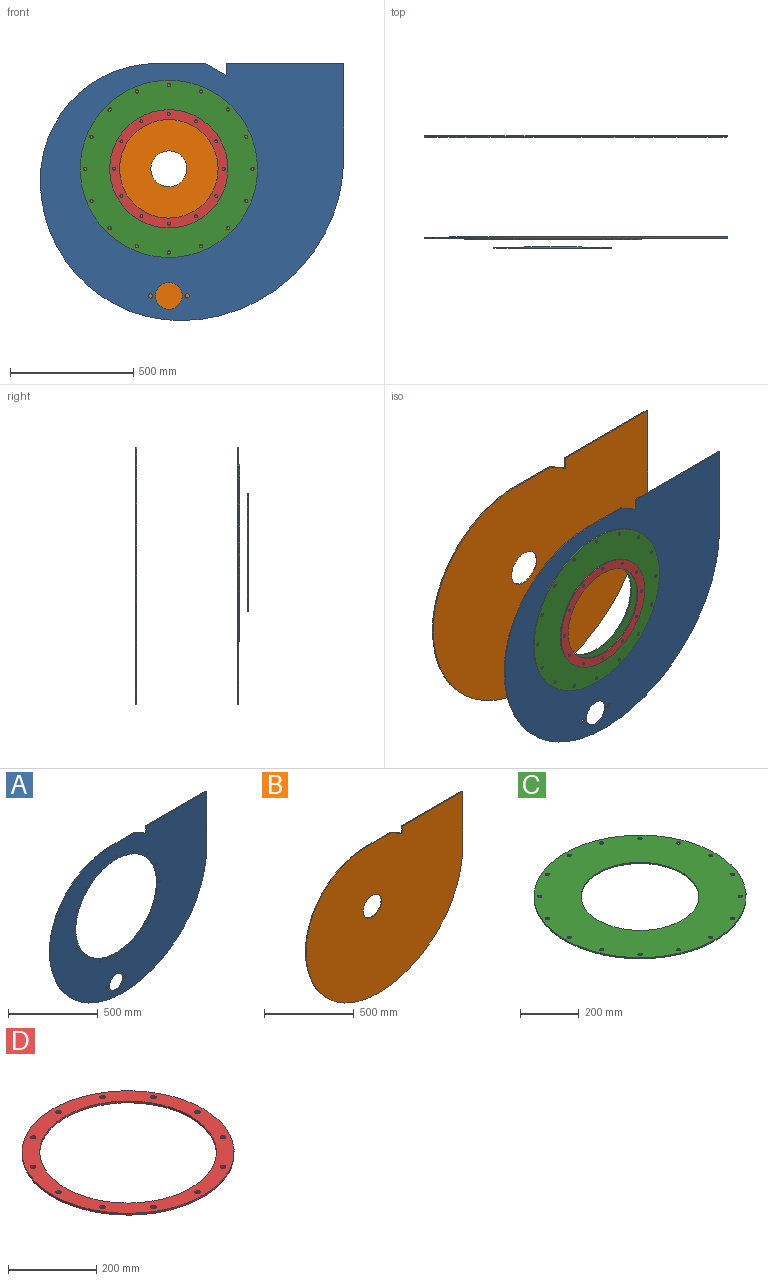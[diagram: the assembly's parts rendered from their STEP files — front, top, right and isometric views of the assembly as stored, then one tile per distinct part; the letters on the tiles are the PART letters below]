
ASSEMBLY  parts=4 mates=4
PART A: 30 faces, bbox 1232x5x1044 mm
  f0: cylinder r=6mm len=12mm, axis (0,1,0), area 188.5mm2, adj f28,f29
  f1: cylinder r=6mm len=12mm, axis (0,1,0), area 188.5mm2, adj f28,f29
  f2: cylinder r=6mm len=12mm, axis (0,1,0), area 188.5mm2, adj f28,f29
  f3: cylinder r=6mm len=12mm, axis (0,1,0), area 188.5mm2, adj f28,f29
  f4: cylinder r=6mm len=12mm, axis (0,1,0), area 188.5mm2, adj f28,f29
  f5: cylinder r=6mm len=12mm, axis (0,1,0), area 188.5mm2, adj f28,f29
  f6: cylinder r=6mm len=12mm, axis (0,1,0), area 188.5mm2, adj f28,f29
  f7: cylinder r=6mm len=12mm, axis (0,1,0), area 188.5mm2, adj f28,f29
  f8: cylinder r=6mm len=12mm, axis (0,1,0), area 188.5mm2, adj f28,f29
  f9: cylinder r=6mm len=12mm, axis (0,1,0), area 188.5mm2, adj f28,f29
  f10: cylinder r=6mm len=12mm, axis (0,1,0), area 188.5mm2, adj f28,f29
  f11: cylinder r=6mm len=12mm, axis (0,1,0), area 188.5mm2, adj f28,f29
  f12: cylinder r=6mm len=12mm, axis (0,1,0), area 188.5mm2, adj f28,f29
  f13: cylinder r=6mm len=12mm, axis (0,1,0), area 188.5mm2, adj f28,f29
  f14: cylinder r=6mm len=12mm, axis (0,1,0), area 188.5mm2, adj f28,f29
  f15: plane 50x5mm, normal (-1,0,0), area 250mm2, adj f16,f26,f28,f29
  f16: plane 86.6x50mm, normal (0.5,0,0.87), area 500mm2, adj f15,f17,f28,f29
  f17: plane 195.4x5mm, normal (0,0,1), area 977mm2, adj f16,f18,f28,f29
  f18: cylinder r=475mm len=475mm, axis (0,1,0), area 3730.6mm2, adj f17,f19,f28,f29
  f19: cylinder r=569mm len=569mm, axis (0,1,0), area 4468.9mm2, adj f18,f20,f28,f29
  f20: cylinder r=663mm len=663mm, axis (0,1,0), area 5207.2mm2, adj f19,f21,f28,f29
  f21: plane 381x5mm, normal (1,0,0), area 1905mm2, adj f20,f26,f28,f29
  f22: cylinder r=6mm len=12mm, axis (0,1,0), area 188.5mm2, adj f28,f29
  f23: cylinder r=54.25mm len=108.5mm, axis (0,1,0), area 1704.3mm2, adj f28,f29
  f24: cylinder r=320mm len=640mm, axis (0,1,0), area 10053.1mm2, adj f28,f29
  f25: cylinder r=8.87mm len=17.73mm, axis (0,1,0), area 278.6mm2, adj f28,f29
  f26: plane 475x5mm, normal (0,0,1), area 2375mm2, adj f15,f21,f28,f29
  f27: cylinder r=8.87mm len=17.73mm, axis (0,1,0), area 278.6mm2, adj f28,f29
  f28: plane 1232x1044mm, normal (0,-1,0), area 738562.8mm2, adj f0,f1,f2,f3,f4,f5,f6,f7
  f29: plane 1232x1044mm, normal (0,1,0), area 738562.8mm2, adj f0,f1,f2,f3,f4,f5,f6,f7
PART B: 11 faces, bbox 1232x5x1044 mm
  f0: plane 50x5mm, normal (-1,0,0), area 250mm2, adj f1,f7,f9,f10
  f1: plane 86.6x50mm, normal (0.5,0,0.87), area 500mm2, adj f0,f2,f9,f10
  f2: plane 195.4x5mm, normal (0,0,1), area 977mm2, adj f1,f3,f9,f10
  f3: cylinder r=475mm len=475mm, axis (0,1,0), area 3730.6mm2, adj f2,f4,f9,f10
  f4: cylinder r=569mm len=569mm, axis (0,1,0), area 4468.9mm2, adj f3,f5,f9,f10
  f5: cylinder r=663mm len=663mm, axis (0,1,0), area 5207.2mm2, adj f4,f6,f9,f10
  f6: plane 381x5mm, normal (1,0,0), area 1905mm2, adj f5,f7,f9,f10
  f7: plane 475x5mm, normal (0,0,1), area 2375mm2, adj f0,f6,f9,f10
  f8: cylinder r=73mm len=146mm, axis (0,1,0), area 2293.4mm2, adj f9,f10
  f9: plane 1232x1044mm, normal (0,-1,0), area 1055069.8mm2, adj f0,f1,f2,f3,f4,f5,f6,f7
  f10: plane 1232x1044mm, normal (0,1,0), area 1055069.8mm2, adj f0,f1,f2,f3,f4,f5,f6,f7
PART C: 20 faces, bbox 720x720x5 mm
  f0: cylinder r=7mm len=14mm, axis (0,0,-1), area 219.9mm2, adj f18,f19
  f1: cylinder r=7mm len=14mm, axis (0,0,-1), area 219.9mm2, adj f18,f19
  f2: cylinder r=7mm len=14mm, axis (0,0,-1), area 219.9mm2, adj f18,f19
  f3: cylinder r=7mm len=14mm, axis (0,0,-1), area 219.9mm2, adj f18,f19
  f4: cylinder r=7mm len=14mm, axis (0,0,-1), area 219.9mm2, adj f18,f19
  f5: cylinder r=7mm len=14mm, axis (0,0,-1), area 219.9mm2, adj f18,f19
  f6: cylinder r=7mm len=14mm, axis (0,0,-1), area 219.9mm2, adj f18,f19
  f7: cylinder r=7mm len=14mm, axis (0,0,-1), area 219.9mm2, adj f18,f19
  f8: cylinder r=7mm len=14mm, axis (0,0,-1), area 219.9mm2, adj f18,f19
  f9: cylinder r=7mm len=14mm, axis (0,0,-1), area 219.9mm2, adj f18,f19
  f10: cylinder r=7mm len=14mm, axis (0,0,-1), area 219.9mm2, adj f18,f19
  f11: cylinder r=7mm len=14mm, axis (0,0,-1), area 219.9mm2, adj f18,f19
  f12: cylinder r=7mm len=14mm, axis (0,0,-1), area 219.9mm2, adj f18,f19
  f13: cylinder r=7mm len=14mm, axis (0,0,-1), area 219.9mm2, adj f18,f19
  f14: cylinder r=7mm len=14mm, axis (0,0,-1), area 219.9mm2, adj f18,f19
  f15: cylinder r=200mm len=400mm, axis (0,0,-1), area 6283.2mm2, adj f18,f19
  f16: cylinder r=7mm len=14mm, axis (0,0,-1), area 219.9mm2, adj f18,f19
  f17: cylinder r=360mm len=720mm, axis (0,0,-1), area 11309.7mm2, adj f18,f19
  f18: plane 720x720mm, normal (0,0,1), area 279023.7mm2, adj f0,f1,f2,f3,f4,f5,f6,f7
  f19: plane 720x720mm, normal (0,0,-1), area 279023.7mm2, adj f0,f1,f2,f3,f4,f5,f6,f7
PART D: 16 faces, bbox 480x480x5 mm
  f0: cylinder r=6mm len=12mm, axis (0,0,-1), area 188.5mm2, adj f14,f15
  f1: cylinder r=6mm len=12mm, axis (0,0,-1), area 188.5mm2, adj f14,f15
  f2: cylinder r=6mm len=12mm, axis (0,0,-1), area 188.5mm2, adj f14,f15
  f3: cylinder r=6mm len=12mm, axis (0,0,-1), area 188.5mm2, adj f14,f15
  f4: cylinder r=6mm len=12mm, axis (0,0,-1), area 188.5mm2, adj f14,f15
  f5: cylinder r=6mm len=12mm, axis (0,0,-1), area 188.5mm2, adj f14,f15
  f6: cylinder r=6mm len=12mm, axis (0,0,-1), area 188.5mm2, adj f14,f15
  f7: cylinder r=6mm len=12mm, axis (0,0,-1), area 188.5mm2, adj f14,f15
  f8: cylinder r=6mm len=12mm, axis (0,0,-1), area 188.5mm2, adj f14,f15
  f9: cylinder r=6mm len=12mm, axis (0,0,-1), area 188.5mm2, adj f14,f15
  f10: cylinder r=6mm len=12mm, axis (0,0,-1), area 188.5mm2, adj f14,f15
  f11: cylinder r=6mm len=12mm, axis (0,0,-1), area 188.5mm2, adj f14,f15
  f12: cylinder r=200mm len=400mm, axis (0,0,-1), area 6283.2mm2, adj f14,f15
  f13: cylinder r=240mm len=480mm, axis (0,0,-1), area 7539.8mm2, adj f14,f15
  f14: plane 480x480mm, normal (0,0,1), area 53934.9mm2, adj f0,f1,f2,f3,f4,f5,f6,f7
  f15: plane 480x480mm, normal (0,0,-1), area 53934.9mm2, adj f0,f1,f2,f3,f4,f5,f6,f7
PLACE A t=(469.61,750.56,-361.78)mm
PLACE B t=(469.61,1161.99,-361.78)mm
PLACE C rot(axis=(1,0,0),90deg) t=(469.61,745.56,-361.78)mm
PLACE D rot(axis=(1,0,0),90deg) t=(469.61,710.01,-361.78)mm
MATE cylindrical D.f12 <-> C.f15  axis (0,-1,0) through (469.61,705.01,-361.78)mm
MATE cylindrical C.f15 <-> A.f24  axis (0,1,0) through (469.61,745.56,-361.78)mm
MATE planar C.f17 <-> A.f28  axis (0,1,0) through (469.61,745.56,-361.78)mm
MATE cylindrical A.f24 <-> B.f8  axis (0,-1,0) through (469.61,745.56,-361.78)mm
